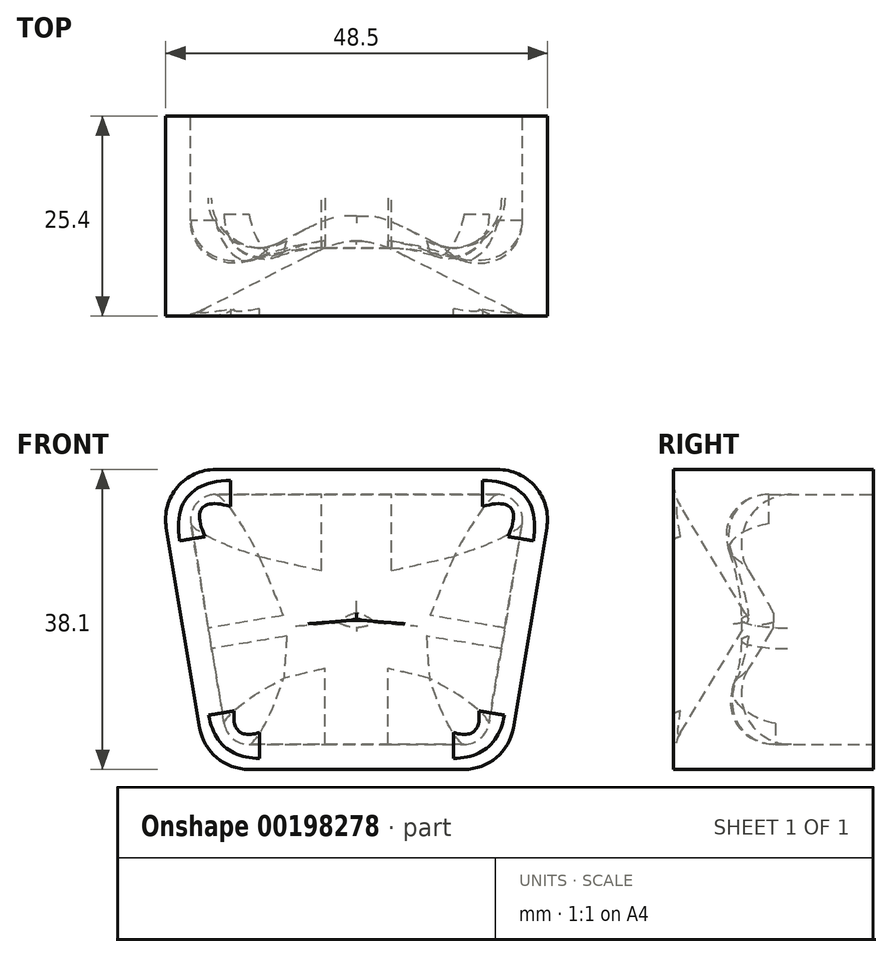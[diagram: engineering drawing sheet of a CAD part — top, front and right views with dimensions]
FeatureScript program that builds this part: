
annotation { "Feature Type Name" : "Feature", "Feature Type Description" : "" }
export const myFeature = defineFeature(function(context is Context, id is Id, definition is map)
    precondition{}
    {
        {
            var Q0;
            Q0=qCreatedBy(makeId("Front.planeOp"),FACE);
            var sketch = newSketch(context, id + "F0", { "sketchPlane" : qUnion([Q0])});
            skLineSegment(sketch, "E0.bottom", {"start": v(13.67, -19.05) * mm, "end": v(-13.67, -19.05) * mm});
            skPoint(sketch, "E0.middle", {"position": v(0, 0) * mm});
            skLineSegment(sketch, "E1", {"start": v(-17.9, 19.05) * mm, "end": v(17.9, 19.05) * mm});
            skLineSegment(sketch, "E2", {"start": v(24.17, 11.66) * mm, "end": v(19.93, -13.74) * mm});
            skLineSegment(sketch, "E3", {"start": v(-24.17, 11.66) * mm, "end": v(-19.93, -13.74) * mm});
            skPoint(sketch, "E4.visualSharp", {"position": v(-25.4, 19.05) * mm});
            skArc(sketch, "E4.filletArc", {"start": v(-17.9, 19.05) * mm, "mid": v(-22.75, 16.8) * mm, "end": v(-24.17, 11.66) * mm});
            skPoint(sketch, "E5.visualSharp", {"position": v(25.4, 19.05) * mm});
            skArc(sketch, "E5.filletArc", {"start": v(24.17, 11.66) * mm, "mid": v(22.75, 16.8) * mm, "end": v(17.9, 19.05) * mm});
            skPoint(sketch, "E6.visualSharp", {"position": v(19.05, -19.05) * mm});
            skArc(sketch, "E6.filletArc", {"start": v(13.67, -19.05) * mm, "mid": v(17.78, -17.55) * mm, "end": v(19.93, -13.74) * mm});
            skPoint(sketch, "E7.visualSharp", {"position": v(-19.05, -19.05) * mm});
            skArc(sketch, "E7.filletArc", {"start": v(-19.93, -13.74) * mm, "mid": v(-17.78, -17.55) * mm, "end": v(-13.67, -19.05) * mm});
            skSolve(sketch);
        }
        {
            var Q0;
            Q0=qSketchRegion(id+"F0",true);
            extrude(context, id + "F1", {"entities" : qUnion([Q0]), "depth" : 25.4 * mm});
        }
        {
            var Q0;
            Q0=makeQuery(id+"F1.opExtrude","CAP_FACE",FACE,{"disambiguationData":[OSD([sQuery(id+"F0.wireOp",EDGE,"E0.bottom"),sQuery(id+"F0.wireOp",EDGE,"E1"),sQuery(id+"F0.wireOp",EDGE,"E2"),sQuery(id+"F0.wireOp",EDGE,"E3"),sQuery(id+"F0.wireOp",EDGE,"E4.filletArc"),sQuery(id+"F0.wireOp",EDGE,"E5.filletArc"),sQuery(id+"F0.wireOp",EDGE,"E6.filletArc"),sQuery(id+"F0.wireOp",EDGE,"E7.filletArc")])],"isStart":false});
            var sketch = newSketch(context, id + "F2", { "sketchPlane" : qUnion([Q0])});
            skLineSegment(sketch, "E8.0.0", {"start": v(-13.67, -19.05) * mm, "end": v(13.67, -19.05) * mm});
            skArc(sketch, "E8.0.1", {"start": v(13.67, -19.05) * mm, "mid": v(17.78, -17.55) * mm, "end": v(19.93, -13.74) * mm});
            skLineSegment(sketch, "E8.0.2", {"start": v(19.93, -13.74) * mm, "end": v(24.17, 11.66) * mm});
            skArc(sketch, "E8.0.3", {"start": v(24.17, 11.66) * mm, "mid": v(22.75, 16.8) * mm, "end": v(17.9, 19.05) * mm});
            skLineSegment(sketch, "E8.0.4", {"start": v(17.9, 19.05) * mm, "end": v(-17.9, 19.05) * mm});
            skArc(sketch, "E8.0.5", {"start": v(-17.9, 19.05) * mm, "mid": v(-22.75, 16.8) * mm, "end": v(-24.17, 11.66) * mm});
            skLineSegment(sketch, "E8.0.6", {"start": v(-24.17, 11.66) * mm, "end": v(-19.93, -13.74) * mm});
            skArc(sketch, "E8.0.7", {"start": v(-19.93, -13.74) * mm, "mid": v(-17.78, -17.55) * mm, "end": v(-13.67, -19.05) * mm});
            skLineSegment(sketch, "E9.0", {"start": v(21.65, 15.88) * mm, "end": v(-21.65, 15.87) * mm});
            skLineSegment(sketch, "E9.1", {"start": v(16.36, -15.88) * mm, "end": v(21.65, 15.88) * mm});
            skLineSegment(sketch, "E9.2", {"start": v(-16.36, -15.88) * mm, "end": v(16.36, -15.88) * mm});
            skLineSegment(sketch, "E9.3", {"start": v(-21.65, 15.88) * mm, "end": v(-16.36, -15.88) * mm});
            skSolve(sketch);
        }
        {
            var Q0;
            Q0=makeQuery(id+"F2.imprint","IMPRINT",FACE,{"disambiguationData":[TD([[makeQuery(id+"F2.imprint","IMPRINT",EDGE,{"derivedFrom":sQuery(id+"F2.wireOp",EDGE,"E9.0")}),1.0]])]});
            extrude(context, id + "F3", {"entities" : qUnion([Q0]), "operationType" : NewBodyOperationType.REMOVE, "oppositeDirection" : true, "depth" : 9.52 * mm});
        }
        {
            var Q0;
            Q0=makeQuery(id+"F3.boolean.opBoolean","COPY",EDGE,{"derivedFrom":makeQuery(id+"F3.opExtrude","CAP_EDGE",EDGE,{"disambiguationData":[OSD([sQuery(id+"F2.wireOp",EDGE,"E9.3")])],"isStart":false})});
            var Q1;
            Q1=makeQuery(id+"F3.boolean.opBoolean","COPY",EDGE,{"derivedFrom":makeQuery(id+"F3.opExtrude","CAP_EDGE",EDGE,{"disambiguationData":[OSD([sQuery(id+"F2.wireOp",EDGE,"E9.0")])],"isStart":false})});
            var Q2;
            Q2=makeQuery(id+"F3.boolean.opBoolean","COPY",EDGE,{"derivedFrom":makeQuery(id+"F3.opExtrude","CAP_EDGE",EDGE,{"disambiguationData":[OSD([sQuery(id+"F2.wireOp",EDGE,"E9.1")])],"isStart":false})});
            var Q3;
            Q3=makeQuery(id+"F3.boolean.opBoolean","COPY",EDGE,{"derivedFrom":makeQuery(id+"F3.opExtrude","CAP_EDGE",EDGE,{"disambiguationData":[OSD([sQuery(id+"F2.wireOp",EDGE,"E9.2")])],"isStart":false})});
            chamfer(context, id + "F4", {"entities" : qUnion([Q0, Q1, Q2, Q3]), "chamferType" : ChamferType.TWO_OFFSETS, "width1" : 15.75 * mm, "oppositeDirection" : false, "width2" : 9.52 * mm, "tangentPropagation" : true});
        }
        {
            var Q0;
            Q0=makeQuery(id+"F4.opChamfer","BLEND_EDGE",EDGE,{"blendedFrom":[makeQuery(id+"F3.boolean.opBoolean","COPY",EDGE,{"derivedFrom":makeQuery(id+"F3.opExtrude","CAP_EDGE",EDGE,{"disambiguationData":[OSD([sQuery(id+"F2.wireOp",EDGE,"E9.0")])],"isStart":false})}),makeQuery(id+"F3.boolean.opBoolean","COPY",EDGE,{"derivedFrom":makeQuery(id+"F3.opExtrude","CAP_EDGE",EDGE,{"disambiguationData":[OSD([sQuery(id+"F2.wireOp",EDGE,"E9.3")])],"isStart":false})})],"blendedInto":[]});
            var Q1;
            Q1=makeQuery(id+"F4.opChamfer","BLEND_EDGE",EDGE,{"blendedFrom":[makeQuery(id+"F3.boolean.opBoolean","COPY",EDGE,{"derivedFrom":makeQuery(id+"F3.opExtrude","CAP_EDGE",EDGE,{"disambiguationData":[OSD([sQuery(id+"F2.wireOp",EDGE,"E9.0")])],"isStart":false})}),makeQuery(id+"F3.boolean.opBoolean","COPY",EDGE,{"derivedFrom":makeQuery(id+"F3.opExtrude","CAP_EDGE",EDGE,{"disambiguationData":[OSD([sQuery(id+"F2.wireOp",EDGE,"E9.1")])],"isStart":false})})],"blendedInto":[]});
            var Q2;
            Q2=makeQuery(id+"F4.opChamfer","BLEND_EDGE",EDGE,{"blendedFrom":[makeQuery(id+"F3.boolean.opBoolean","COPY",EDGE,{"derivedFrom":makeQuery(id+"F3.opExtrude","CAP_EDGE",EDGE,{"disambiguationData":[OSD([sQuery(id+"F2.wireOp",EDGE,"E9.2")])],"isStart":false})}),makeQuery(id+"F3.boolean.opBoolean","COPY",EDGE,{"derivedFrom":makeQuery(id+"F3.opExtrude","CAP_EDGE",EDGE,{"disambiguationData":[OSD([sQuery(id+"F2.wireOp",EDGE,"E9.3")])],"isStart":false})})],"blendedInto":[]});
            var Q3;
            Q3=makeQuery(id+"F4.opChamfer","BLEND_EDGE",EDGE,{"blendedFrom":[makeQuery(id+"F3.boolean.opBoolean","COPY",EDGE,{"derivedFrom":makeQuery(id+"F3.opExtrude","CAP_EDGE",EDGE,{"disambiguationData":[OSD([sQuery(id+"F2.wireOp",EDGE,"E9.1")])],"isStart":false})}),makeQuery(id+"F3.boolean.opBoolean","COPY",EDGE,{"derivedFrom":makeQuery(id+"F3.opExtrude","CAP_EDGE",EDGE,{"disambiguationData":[OSD([sQuery(id+"F2.wireOp",EDGE,"E9.2")])],"isStart":false})})],"blendedInto":[]});
            fillet(context, id + "F5", {"entities" : qUnion([Q0, Q1, Q2, Q3]), "radius" : 6.35 * mm, "tangentPropagation" : true, "allowEdgeOverflow" : false});
        }
        {
            var Q0;
            Q0=makeQuery(id+"F4.opChamfer","BLEND_EDGE",EDGE,{"blendedFrom":[makeQuery(id+"F3.boolean.opBoolean","COPY",EDGE,{"derivedFrom":makeQuery(id+"F3.opExtrude","CAP_EDGE",EDGE,{"disambiguationData":[OSD([sQuery(id+"F2.wireOp",EDGE,"E9.3")])],"isStart":false})}),makeQuery(id+"F1.opExtrude","CAP_FACE",FACE,{"disambiguationData":[OSD([sQuery(id+"F0.wireOp",EDGE,"E0.bottom"),sQuery(id+"F0.wireOp",EDGE,"E1"),sQuery(id+"F0.wireOp",EDGE,"E2"),sQuery(id+"F0.wireOp",EDGE,"E3"),sQuery(id+"F0.wireOp",EDGE,"E4.filletArc"),sQuery(id+"F0.wireOp",EDGE,"E5.filletArc"),sQuery(id+"F0.wireOp",EDGE,"E6.filletArc"),sQuery(id+"F0.wireOp",EDGE,"E7.filletArc")])],"isStart":false})],"blendedInto":[makeQuery(id+"F1.opExtrude","CAP_FACE",FACE,{"disambiguationData":[OSD([sQuery(id+"F0.wireOp",EDGE,"E0.bottom"),sQuery(id+"F0.wireOp",EDGE,"E1"),sQuery(id+"F0.wireOp",EDGE,"E2"),sQuery(id+"F0.wireOp",EDGE,"E3"),sQuery(id+"F0.wireOp",EDGE,"E4.filletArc"),sQuery(id+"F0.wireOp",EDGE,"E5.filletArc"),sQuery(id+"F0.wireOp",EDGE,"E6.filletArc"),sQuery(id+"F0.wireOp",EDGE,"E7.filletArc")])],"isStart":false})]});
            fillet(context, id + "F6", {"entities" : qUnion([Q0]), "radius" : 6.35 * mm, "tangentPropagation" : true, "allowEdgeOverflow" : false});
        }
        {
            var Q0;
            Q0=makeQuery(id+"F1.opExtrude","CAP_FACE",FACE,{"disambiguationData":[OSD([sQuery(id+"F0.wireOp",EDGE,"E0.bottom"),sQuery(id+"F0.wireOp",EDGE,"E1"),sQuery(id+"F0.wireOp",EDGE,"E2"),sQuery(id+"F0.wireOp",EDGE,"E3"),sQuery(id+"F0.wireOp",EDGE,"E4.filletArc"),sQuery(id+"F0.wireOp",EDGE,"E5.filletArc"),sQuery(id+"F0.wireOp",EDGE,"E6.filletArc"),sQuery(id+"F0.wireOp",EDGE,"E7.filletArc")])],"isStart":true});
            shell(context, id + "F7", {"entities" : qUnion([Q0]), "thickness" : 3.17 * mm});
        }
        {
            var Q0;
            Q0=makeQuery(id+"F7.opShell","TWEAK_EDGE",EDGE,{"derivedFrom":[makeQuery(id+"F1.opExtrude","SWEPT_FACE",FACE,{"disambiguationData":[OSD([sQuery(id+"F0.wireOp",EDGE,"E1")])]}),makeQuery(id+"F4.opChamfer","BLEND_FACE",FACE,{"disambiguationData":[OSD([sQuery(id+"F2.wireOp",EDGE,"E9.0")])]})]});
            fillet(context, id + "F8", {"entities" : qUnion([Q0]), "radius" : 6.35 * mm, "tangentPropagation" : true, "allowEdgeOverflow" : false});
        }
    });
